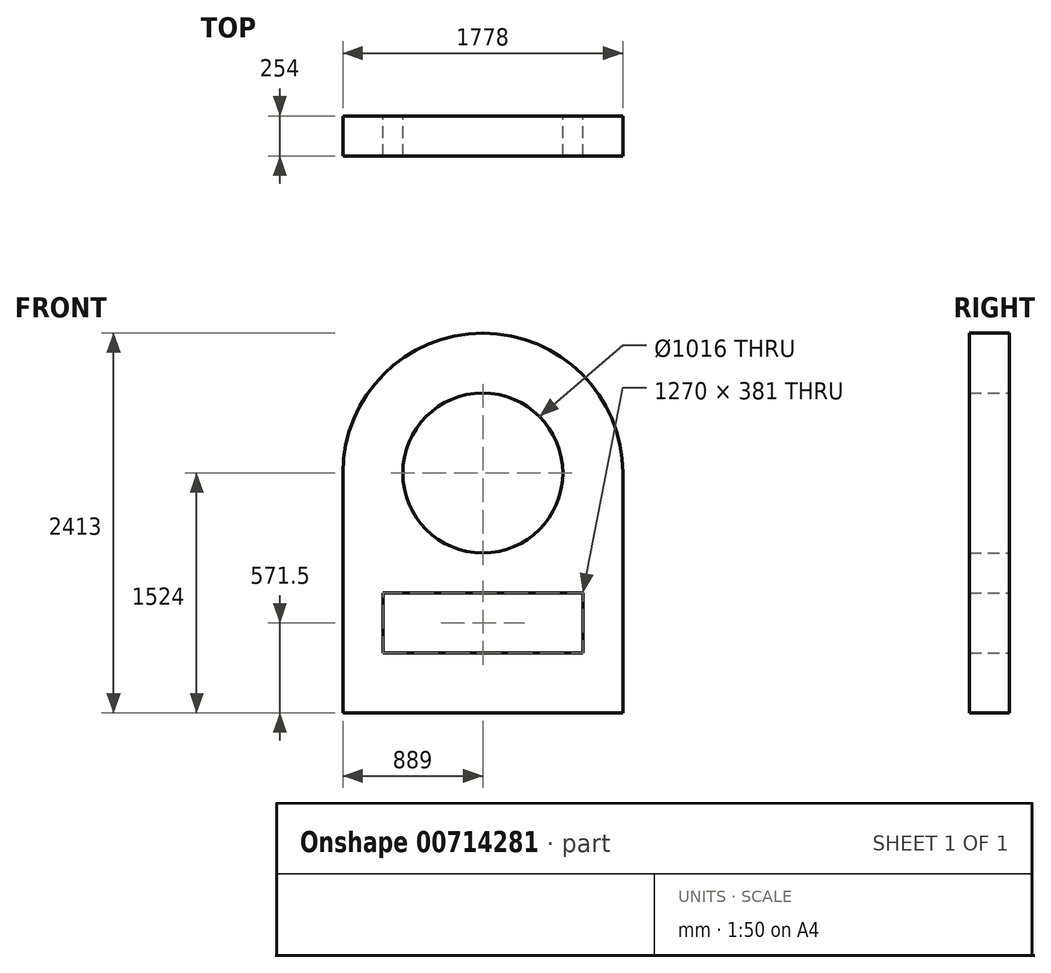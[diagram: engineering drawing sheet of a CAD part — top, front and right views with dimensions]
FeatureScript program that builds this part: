
annotation { "Feature Type Name" : "Feature", "Feature Type Description" : "" }
export const myFeature = defineFeature(function(context is Context, id is Id, definition is map)
    precondition{}
    {
        {
            var Q0;
            Q0=qCreatedBy(makeId("Front.planeOp"),FACE);
            var sketch = newSketch(context, id + "F0", { "sketchPlane" : qUnion([Q0])});
            skCircle(sketch, "E0", {"center": v(0, 0) * mm, "radius": 508 * mm});
            skArc(sketch, "E1", {"start": v(889, 0) * mm, "mid": v(0, 889) * mm, "end": v(-889, 0) * mm});
            skLineSegment(sketch, "E2", {"start": v(-889, 0) * mm, "end": v(-889, -1524) * mm});
            skLineSegment(sketch, "E3", {"start": v(-889, -1524) * mm, "end": v(889, -1524) * mm});
            skLineSegment(sketch, "E4", {"start": v(889, -1524) * mm, "end": v(889, 0) * mm});
            skLineSegment(sketch, "E5.bottom", {"start": v(-635, -1143) * mm, "end": v(635, -1143) * mm});
            skLineSegment(sketch, "E5.top", {"start": v(-635, -762) * mm, "end": v(635, -762) * mm});
            skLineSegment(sketch, "E5.left", {"start": v(-635, -1143) * mm, "end": v(-635, -762) * mm});
            skLineSegment(sketch, "E5.right", {"start": v(635, -1143) * mm, "end": v(635, -762) * mm});
            skSolve(sketch);
        }
        {
            var Q0;
            Q0=makeQuery(id+"F0.imprint","IMPRINT",FACE,{"disambiguationData":[TD([[makeQuery(id+"F0.imprint","IMPRINT",EDGE,{"derivedFrom":sQuery(id+"F0.wireOp",EDGE,"E0")}),-1.0]])]});
            extrude(context, id + "F1", {"entities" : qUnion([Q0]), "depth" : 254 * mm, "offsetDistance" : 25.4 * mm});
        }
    });
